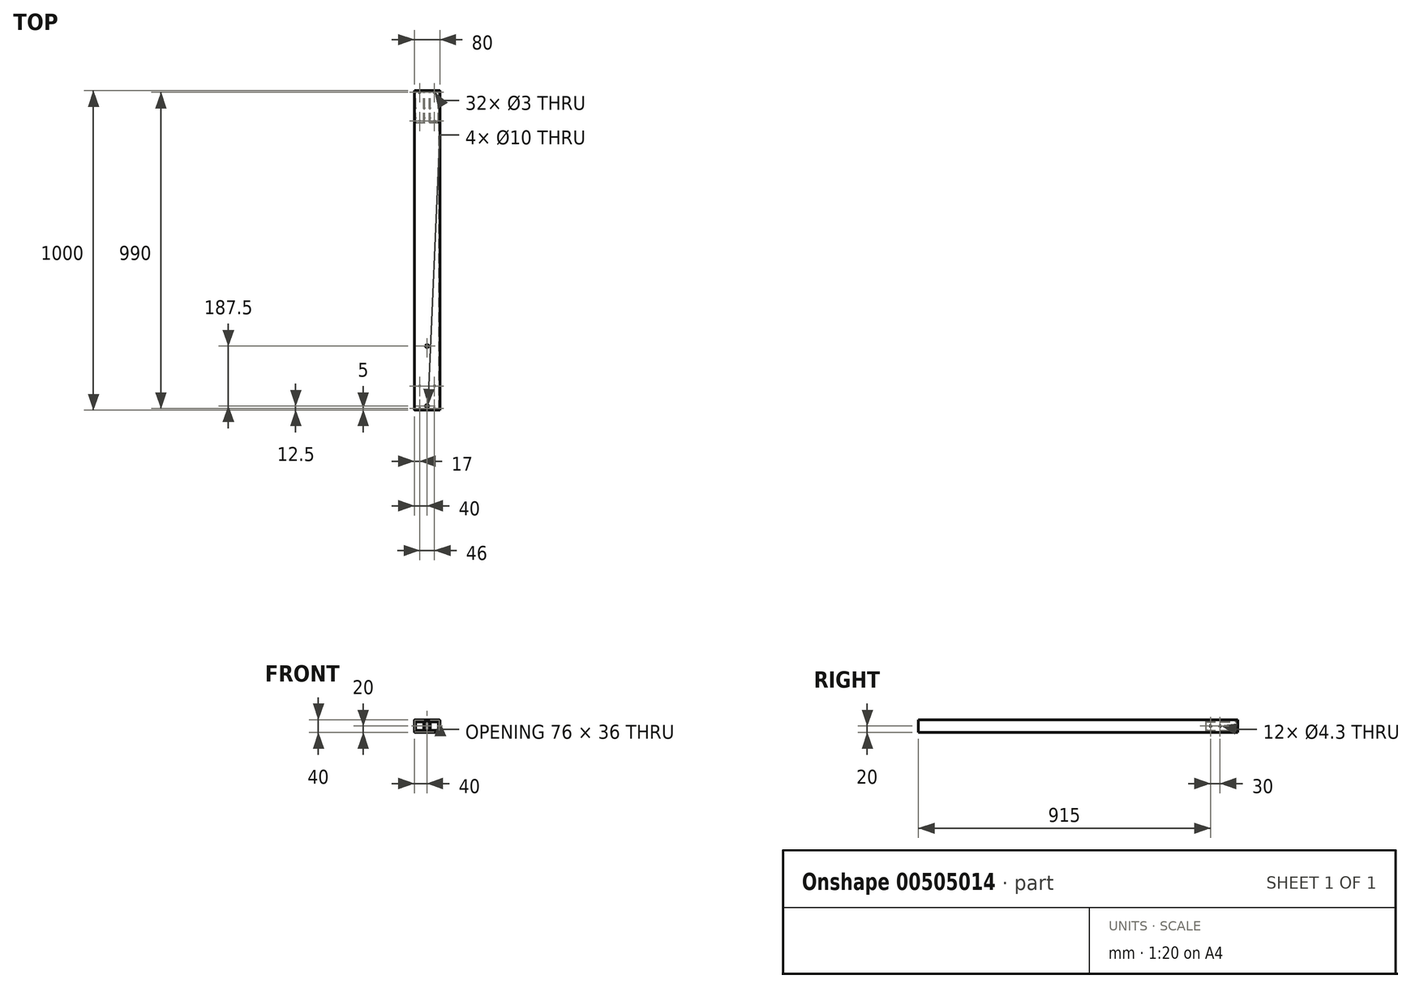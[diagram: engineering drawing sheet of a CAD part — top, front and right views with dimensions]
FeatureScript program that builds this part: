
annotation { "Feature Type Name" : "Feature", "Feature Type Description" : "" }
export const myFeature = defineFeature(function(context is Context, id is Id, definition is map)
    precondition{}
    {
        {
            var Q0;
            Q0=qCreatedBy(makeId("Front.planeOp"),FACE);
            var sketch = newSketch(context, id + "F0", { "sketchPlane" : qUnion([Q0])});
            skLineSegment(sketch, "E0.bottom", {"start": v(-38, 20) * mm, "end": v(38, 20) * mm});
            skLineSegment(sketch, "E0.top", {"start": v(-38, -20) * mm, "end": v(38, -20) * mm});
            skLineSegment(sketch, "E0.left", {"start": v(-40, 18) * mm, "end": v(-40, -18) * mm});
            skLineSegment(sketch, "E0.right", {"start": v(40, 18) * mm, "end": v(40, -18) * mm});
            skPoint(sketch, "E1.visualSharp", {"position": v(-38, 18) * mm});
            skPoint(sketch, "E2.visualSharp", {"position": v(38, -18) * mm});
            skPoint(sketch, "E3.visualSharp", {"position": v(-38, -18) * mm});
            skPoint(sketch, "E4.visualSharp", {"position": v(-40, 20) * mm});
            skArc(sketch, "E4.filletArc", {"start": v(-38, 20) * mm, "mid": v(-39.41, 19.41) * mm, "end": v(-40, 18) * mm});
            skPoint(sketch, "E5.visualSharp", {"position": v(40, 20) * mm});
            skArc(sketch, "E5.filletArc", {"start": v(40, 18) * mm, "mid": v(39.41, 19.41) * mm, "end": v(38, 20) * mm});
            skPoint(sketch, "E6.visualSharp", {"position": v(40, -20) * mm});
            skArc(sketch, "E6.filletArc", {"start": v(38, -20) * mm, "mid": v(39.41, -19.41) * mm, "end": v(40, -18) * mm});
            skPoint(sketch, "E7.visualSharp", {"position": v(-40, -20) * mm});
            skArc(sketch, "E7.filletArc", {"start": v(-40, -18) * mm, "mid": v(-39.41, -19.41) * mm, "end": v(-38, -20) * mm});
            skLineSegment(sketch, "E8.bottom", {"start": v(-37, 18) * mm, "end": v(37, 18) * mm});
            skLineSegment(sketch, "E8.top", {"start": v(-37, -18) * mm, "end": v(37, -18) * mm});
            skLineSegment(sketch, "E8.left", {"start": v(-38, 17) * mm, "end": v(-38, -17) * mm});
            skLineSegment(sketch, "E8.right", {"start": v(38, 17) * mm, "end": v(38, -17) * mm});
            skArc(sketch, "E9.filletArc", {"start": v(-37, 18) * mm, "mid": v(-37.7, 17.7) * mm, "end": v(-38, 17) * mm});
            skArc(sketch, "E10.filletArc", {"start": v(-38, -17) * mm, "mid": v(-37.7, -17.7) * mm, "end": v(-37, -18) * mm});
            skArc(sketch, "E11.filletArc", {"start": v(37, -18) * mm, "mid": v(37.7, -17.7) * mm, "end": v(38, -17) * mm});
            skArc(sketch, "E12.filletArc", {"start": v(38, 17) * mm, "mid": v(37.7, 17.7) * mm, "end": v(37, 18) * mm});
            skPoint(sketch, "E13", {"position": v(0, 0) * mm});
            skSolve(sketch);
        }
        {
            var Q0;
            Q0=makeQuery(id+"F0.imprint","IMPRINT",FACE,{"disambiguationData":[TD([[makeQuery(id+"F0.imprint","IMPRINT",EDGE,{"derivedFrom":sQuery(id+"F0.wireOp",EDGE,"E0.bottom")}),-1.0]])]});
            var Q1;
            {var subQ0=sQuery(id+"F0.wireOp",EDGE,"d41scRek-im4C-Z6XJ-NA7b-lybMWtBvQDZa.bottom");var subQ1=sQuery(id+"F0.wireOp",EDGE,"E1.filletArc");var subQ2=makeQuery(id+"F0.imprint","INTERSECT",VERTEX,{"derivedFrom":[subQ1,subQ0]});Q1=makeQuery(id+"F0.imprint","IMPRINT",FACE,{"disambiguationData":[TD([[makeQuery(id+"F0.imprint","IMPRINT",EDGE,{"disambiguationData":[TD([[subQ2,-1.0]])],"derivedFrom":subQ1}),-1.0]])]});}
            var Q2;
            {var subQ0=sQuery(id+"F0.wireOp",EDGE,"d41scRek-im4C-Z6XJ-NA7b-lybMWtBvQDZa.right");var subQ1=sQuery(id+"F0.wireOp",EDGE,"49b38d49-dcaf-4ad4-8bbf-e22f50cbbb73.filletArc");var subQ2=makeQuery(id+"F0.imprint","INTERSECT",VERTEX,{"derivedFrom":[subQ1,subQ0]});Q2=makeQuery(id+"F0.imprint","IMPRINT",FACE,{"disambiguationData":[TD([[makeQuery(id+"F0.imprint","IMPRINT",EDGE,{"disambiguationData":[TD([[subQ2,-1.0]])],"derivedFrom":subQ1}),-1.0]])]});}
            var Q3;
            {var subQ0=sQuery(id+"F0.wireOp",EDGE,"7cdcf8cc-6b16-4f10-b10a-e8f9950829020.MirrorCS");var subQ1=sQuery(id+"F0.wireOp",EDGE,"E2.filletArc");var subQ2=makeQuery(id+"F0.imprint","INTERSECT",VERTEX,{"derivedFrom":[subQ1,subQ0]});Q3=makeQuery(id+"F0.imprint","IMPRINT",FACE,{"disambiguationData":[TD([[makeQuery(id+"F0.imprint","IMPRINT",EDGE,{"disambiguationData":[TD([[subQ2,-1.0]])],"derivedFrom":subQ1}),-1.0]])]});}
            var Q4;
            {var subQ0=sQuery(id+"F0.wireOp",EDGE,"daf54ab9-f530-4c55-a2cd-1cfbda922d990.MirrorCS");var subQ1=sQuery(id+"F0.wireOp",EDGE,"E3.filletArc");var subQ2=makeQuery(id+"F0.imprint","INTERSECT",VERTEX,{"derivedFrom":[subQ1,subQ0]});Q4=makeQuery(id+"F0.imprint","IMPRINT",FACE,{"disambiguationData":[TD([[makeQuery(id+"F0.imprint","IMPRINT",EDGE,{"disambiguationData":[TD([[subQ2,-1.0]])],"derivedFrom":subQ1}),-1.0]])]});}
            var Q5;
            {var subQ4=sQuery(id+"F0.wireOp",EDGE,"E0.right");Q5=makeQuery(id+"F0.imprint","IMPRINT",FACE,{"disambiguationData":[TD([[makeQuery(id+"F0.imprint","IMPRINT",EDGE,{"derivedFrom":subQ4}),-1.0]])]});}
            var Q6;
            {var subQ1=sQuery(id+"F0.wireOp",EDGE,"E0.top");Q6=makeQuery(id+"F0.imprint","IMPRINT",FACE,{"disambiguationData":[TD([[makeQuery(id+"F0.imprint","IMPRINT",EDGE,{"derivedFrom":subQ1}),1.0]])]});}
            var Q7;
            {var subQ1=sQuery(id+"F0.wireOp",EDGE,"E0.left");Q7=makeQuery(id+"F0.imprint","IMPRINT",FACE,{"disambiguationData":[TD([[makeQuery(id+"F0.imprint","IMPRINT",EDGE,{"derivedFrom":subQ1}),1.0]])]});}
            extrude(context, id + "F1", {"entities" : qUnion([Q0, Q1, Q2, Q3, Q4, Q5, Q6, Q7]), "depth" : 1000 * mm, "offsetDistance" : 25 * mm});
        }
        {
            var Q0;
            Q0=qCreatedBy(makeId("Front.planeOp"),FACE);
            cPlane(context, id + "F2", {"entities" : qUnion([Q0]), "cplaneType" : CPlaneType.OFFSET, "offset" : 1000 * mm, "width" : 150 * mm, "height" : 150 * mm});
        }
        {
            var Q0;
            Q0=qCreatedBy(makeId("Right.planeOp"),FACE);
            var sketch = newSketch(context, id + "F3", { "sketchPlane" : qUnion([Q0])});
            skPoint(sketch, "E14", {"position": v(-1000, 0) * mm});
            skSolve(sketch);
        }
        {
            var Q0;
            Q0=qCreatedBy(makeId("Front.planeOp"),FACE);
            var sketch = newSketch(context, id + "F4", { "sketchPlane" : qUnion([Q0])});
            skLineSegment(sketch, "E15.bottom", {"start": v(-36.5, 18) * mm, "end": v(36.5, 18) * mm});
            skLineSegment(sketch, "E15.top", {"start": v(-36.5, 15) * mm, "end": v(36.5, 15) * mm});
            skLineSegment(sketch, "E15.left", {"start": v(-38, 16.5) * mm, "end": v(-38, 16.5) * mm});
            skLineSegment(sketch, "E15.right", {"start": v(38, 16.5) * mm, "end": v(38, 16.5) * mm});
            skPoint(sketch, "E16.visualSharp", {"position": v(-38, 18) * mm});
            skArc(sketch, "E16.filletArc", {"start": v(-36.5, 18) * mm, "mid": v(-37.56, 17.56) * mm, "end": v(-38, 16.5) * mm});
            skPoint(sketch, "E17.visualSharp", {"position": v(-38, 15) * mm});
            skArc(sketch, "E17.filletArc", {"start": v(-38, 16.5) * mm, "mid": v(-37.56, 15.44) * mm, "end": v(-36.5, 15) * mm});
            skPoint(sketch, "E18.visualSharp", {"position": v(38, 18) * mm});
            skArc(sketch, "E18.filletArc", {"start": v(38, 16.5) * mm, "mid": v(37.56, 17.56) * mm, "end": v(36.5, 18) * mm});
            skPoint(sketch, "E19.visualSharp", {"position": v(38, 15) * mm});
            skArc(sketch, "E19.filletArc", {"start": v(36.5, 15) * mm, "mid": v(37.56, 15.44) * mm, "end": v(38, 16.5) * mm});
            skLineSegment(sketch, "E20.MirrorCS", {"start": v(-36.5, -18) * mm, "end": v(36.5, -18) * mm});
            skArc(sketch, "E21.MirrorCS", {"start": v(-36.5, -18) * mm, "mid": v(-37.56, -17.56) * mm, "end": v(-38, -16.5) * mm});
            skArc(sketch, "E22.MirrorCS", {"start": v(-38, -16.5) * mm, "mid": v(-37.56, -15.44) * mm, "end": v(-36.5, -15) * mm});
            skLineSegment(sketch, "E23.MirrorCS", {"start": v(-36.5, -15) * mm, "end": v(36.5, -15) * mm});
            skArc(sketch, "E24.MirrorCS", {"start": v(36.5, -15) * mm, "mid": v(37.56, -15.44) * mm, "end": v(38, -16.5) * mm});
            skArc(sketch, "E25.MirrorCS", {"start": v(38, -16.5) * mm, "mid": v(37.56, -17.56) * mm, "end": v(36.5, -18) * mm});
            skSolve(sketch);
        }
        {
            var Q0;
            Q0=makeQuery(id+"F4.imprint","IMPRINT",FACE,{"disambiguationData":[TD([[makeQuery(id+"F4.imprint","IMPRINT",EDGE,{"derivedFrom":sQuery(id+"F4.wireOp",EDGE,"E15.bottom")}),-1.0]])]});
            var Q1;
            Q1=makeQuery(id+"F4.imprint","IMPRINT",FACE,{"disambiguationData":[TD([[makeQuery(id+"F4.imprint","IMPRINT",EDGE,{"derivedFrom":sQuery(id+"F4.wireOp",EDGE,"E20.MirrorCS")}),1.0]])]});
            extrude(context, id + "F5", {"entities" : qUnion([Q0, Q1]), "depth" : 100 * mm, "offsetDistance" : 25 * mm});
        }
        {
            var Q0;
            Q0=qCreatedBy(makeId("Front.planeOp"),FACE);
            var sketch = newSketch(context, id + "F6", { "sketchPlane" : qUnion([Q0])});
            skLineSegment(sketch, "E26.bottom", {"start": v(-36, 15) * mm, "end": v(-10, 15) * mm});
            skLineSegment(sketch, "E26.top", {"start": v(-36, -15) * mm, "end": v(-10, -15) * mm});
            skLineSegment(sketch, "E26.left", {"start": v(-38, 13) * mm, "end": v(-38, -13) * mm});
            skLineSegment(sketch, "E26.right", {"start": v(-8, 13) * mm, "end": v(-8, -13) * mm});
            skPoint(sketch, "E27.visualSharp", {"position": v(-38, 15) * mm});
            skArc(sketch, "E27.filletArc", {"start": v(-36, 15) * mm, "mid": v(-37.41, 14.41) * mm, "end": v(-38, 13) * mm});
            skPoint(sketch, "E28.visualSharp", {"position": v(-8, 15) * mm});
            skArc(sketch, "E28.filletArc", {"start": v(-8, 13) * mm, "mid": v(-8.59, 14.41) * mm, "end": v(-10, 15) * mm});
            skPoint(sketch, "E29.visualSharp", {"position": v(-8, -15) * mm});
            skArc(sketch, "E29.filletArc", {"start": v(-10, -15) * mm, "mid": v(-8.59, -14.41) * mm, "end": v(-8, -13) * mm});
            skPoint(sketch, "E30.visualSharp", {"position": v(-38, -15) * mm});
            skArc(sketch, "E30.filletArc", {"start": v(-38, -13) * mm, "mid": v(-37.41, -14.41) * mm, "end": v(-36, -15) * mm});
            skLineSegment(sketch, "E31.0", {"start": v(-35, 13) * mm, "end": v(-11, 13) * mm});
            skLineSegment(sketch, "E31.1", {"start": v(-36, 12) * mm, "end": v(-36, -12) * mm});
            skLineSegment(sketch, "E31.2", {"start": v(-35, -13) * mm, "end": v(-11, -13) * mm});
            skLineSegment(sketch, "E31.3", {"start": v(-10, 12) * mm, "end": v(-10, -12) * mm});
            skArc(sketch, "E32.filletArc", {"start": v(-35, 13) * mm, "mid": v(-35.7, 12.7) * mm, "end": v(-36, 12) * mm});
            skArc(sketch, "E33.filletArc", {"start": v(-10, 12) * mm, "mid": v(-10.3, 12.7) * mm, "end": v(-11, 13) * mm});
            skArc(sketch, "E34.filletArc", {"start": v(-11, -13) * mm, "mid": v(-10.3, -12.7) * mm, "end": v(-10, -12) * mm});
            skArc(sketch, "E35.filletArc", {"start": v(-36, -12) * mm, "mid": v(-35.7, -12.7) * mm, "end": v(-35, -13) * mm});
            skLineSegment(sketch, "E36.MirrorCS", {"start": v(8, 13) * mm, "end": v(8, -13) * mm});
            skArc(sketch, "E37.MirrorCS", {"start": v(8, 13) * mm, "mid": v(8.59, 14.41) * mm, "end": v(10, 15) * mm});
            skLineSegment(sketch, "E38.MirrorCS", {"start": v(36, 15) * mm, "end": v(10, 15) * mm});
            skArc(sketch, "E39.MirrorCS", {"start": v(36, 15) * mm, "mid": v(37.41, 14.41) * mm, "end": v(38, 13) * mm});
            skLineSegment(sketch, "E40.MirrorCS", {"start": v(38, 13) * mm, "end": v(38, -13) * mm});
            skArc(sketch, "E41.MirrorCS", {"start": v(38, -13) * mm, "mid": v(37.41, -14.41) * mm, "end": v(36, -15) * mm});
            skLineSegment(sketch, "E42.MirrorCS", {"start": v(36, -15) * mm, "end": v(10, -15) * mm});
            skArc(sketch, "E43.MirrorCS", {"start": v(10, -15) * mm, "mid": v(8.59, -14.41) * mm, "end": v(8, -13) * mm});
            skArc(sketch, "E44.MirrorCS", {"start": v(11, -13) * mm, "mid": v(10.3, -12.7) * mm, "end": v(10, -12) * mm});
            skLineSegment(sketch, "E45.MirrorCS", {"start": v(10, 12) * mm, "end": v(10, -12) * mm});
            skArc(sketch, "E46.MirrorCS", {"start": v(10, 12) * mm, "mid": v(10.3, 12.7) * mm, "end": v(11, 13) * mm});
            skLineSegment(sketch, "E47.MirrorCS", {"start": v(35, 13) * mm, "end": v(11, 13) * mm});
            skArc(sketch, "E48.MirrorCS", {"start": v(35, 13) * mm, "mid": v(35.7, 12.7) * mm, "end": v(36, 12) * mm});
            skLineSegment(sketch, "E49.MirrorCS", {"start": v(36, 12) * mm, "end": v(36, -12) * mm});
            skArc(sketch, "E50.MirrorCS", {"start": v(36, -12) * mm, "mid": v(35.7, -12.7) * mm, "end": v(35, -13) * mm});
            skLineSegment(sketch, "E51.MirrorCS", {"start": v(35, -13) * mm, "end": v(11, -13) * mm});
            skSolve(sketch);
        }
        {
            var Q0;
            Q0=makeQuery(id+"F6.imprint","IMPRINT",FACE,{"disambiguationData":[TD([[makeQuery(id+"F6.imprint","IMPRINT",EDGE,{"derivedFrom":sQuery(id+"F6.wireOp",EDGE,"E26.bottom")}),-1.0]])]});
            var Q1;
            Q1=makeQuery(id+"F6.imprint","IMPRINT",FACE,{"disambiguationData":[TD([[makeQuery(id+"F6.imprint","IMPRINT",EDGE,{"derivedFrom":sQuery(id+"F6.wireOp",EDGE,"E36.MirrorCS")}),1.0]])]});
            extrude(context, id + "F7", {"entities" : qUnion([Q0, Q1]), "depth" : 100 * mm, "offsetDistance" : 25 * mm});
        }
        {
            var Q0;
            Q0=makeQuery(id+"F7.opExtrude","CAP_FACE",FACE,{"disambiguationData":[OSD([sQuery(id+"F6.wireOp",EDGE,"E26.bottom"),sQuery(id+"F6.wireOp",EDGE,"E26.top"),sQuery(id+"F6.wireOp",EDGE,"E26.left"),sQuery(id+"F6.wireOp",EDGE,"E26.right"),sQuery(id+"F6.wireOp",EDGE,"E27.filletArc"),sQuery(id+"F6.wireOp",EDGE,"E28.filletArc"),sQuery(id+"F6.wireOp",EDGE,"E29.filletArc"),sQuery(id+"F6.wireOp",EDGE,"E30.filletArc"),sQuery(id+"F6.wireOp",EDGE,"E31.0"),sQuery(id+"F6.wireOp",EDGE,"E31.1"),sQuery(id+"F6.wireOp",EDGE,"E31.2"),sQuery(id+"F6.wireOp",EDGE,"E31.3"),sQuery(id+"F6.wireOp",EDGE,"E32.filletArc"),sQuery(id+"F6.wireOp",EDGE,"E33.filletArc"),sQuery(id+"F6.wireOp",EDGE,"E34.filletArc"),sQuery(id+"F6.wireOp",EDGE,"E35.filletArc")])],"isStart":false});
            var Q1;
            Q1=makeQuery(id+"F7.opExtrude","CAP_FACE",FACE,{"disambiguationData":[OSD([sQuery(id+"F6.wireOp",EDGE,"E36.MirrorCS"),sQuery(id+"F6.wireOp",EDGE,"E37.MirrorCS"),sQuery(id+"F6.wireOp",EDGE,"E38.MirrorCS"),sQuery(id+"F6.wireOp",EDGE,"E39.MirrorCS"),sQuery(id+"F6.wireOp",EDGE,"E40.MirrorCS"),sQuery(id+"F6.wireOp",EDGE,"E41.MirrorCS"),sQuery(id+"F6.wireOp",EDGE,"E42.MirrorCS"),sQuery(id+"F6.wireOp",EDGE,"E43.MirrorCS"),sQuery(id+"F6.wireOp",EDGE,"E44.MirrorCS"),sQuery(id+"F6.wireOp",EDGE,"E45.MirrorCS"),sQuery(id+"F6.wireOp",EDGE,"E46.MirrorCS"),sQuery(id+"F6.wireOp",EDGE,"E47.MirrorCS"),sQuery(id+"F6.wireOp",EDGE,"E48.MirrorCS"),sQuery(id+"F6.wireOp",EDGE,"E49.MirrorCS"),sQuery(id+"F6.wireOp",EDGE,"E50.MirrorCS"),sQuery(id+"F6.wireOp",EDGE,"E51.MirrorCS")])],"isStart":false});
            var Q2;
            Q2=makeQuery(id+"F5.opExtrude","CAP_FACE",FACE,{"disambiguationData":[OSD([sQuery(id+"F4.wireOp",EDGE,"E15.bottom"),sQuery(id+"F4.wireOp",EDGE,"E15.top"),sQuery(id+"F4.wireOp",EDGE,"E16.filletArc"),sQuery(id+"F4.wireOp",EDGE,"E17.filletArc"),sQuery(id+"F4.wireOp",EDGE,"E18.filletArc"),sQuery(id+"F4.wireOp",EDGE,"E19.filletArc")])],"isStart":false});
            var Q3;
            Q3=makeQuery(id+"F5.opExtrude","CAP_FACE",FACE,{"disambiguationData":[OSD([sQuery(id+"F4.wireOp",EDGE,"E20.MirrorCS"),sQuery(id+"F4.wireOp",EDGE,"E21.MirrorCS"),sQuery(id+"F4.wireOp",EDGE,"E22.MirrorCS"),sQuery(id+"F4.wireOp",EDGE,"E23.MirrorCS"),sQuery(id+"F4.wireOp",EDGE,"E24.MirrorCS"),sQuery(id+"F4.wireOp",EDGE,"E25.MirrorCS")])],"isStart":false});
            fillet(context, id + "F8", {"entities" : qUnion([Q0, Q1, Q2, Q3]), "radius" : 0.5 * mm, "tangentPropagation" : true, "allowEdgeOverflow" : false});
        }
        {
            var Q0;
            Q0=makeQuery(id+"F1.opExtrude","SWEPT_FACE",FACE,{"disambiguationData":[OSD([sQuery(id+"F0.wireOp",EDGE,"E0.right")])]});
            var sketch = newSketch(context, id + "F9", { "sketchPlane" : qUnion([Q0])});
            skLineSegment(sketch, "E52", {"start": v(0, 0) * mm, "end": v(-85, 0) * mm, "construction": true});
            skCircle(sketch, "E53", {"center": v(-85, 0) * mm, "radius": 2.15 * mm});
            skCircle(sketch, "E54", {"center": v(-55, 0) * mm, "radius": 2.15 * mm});
            skPoint(sketch, "E55.centerSnap0", {"position": v(-1000, 0) * mm});
            skSolve(sketch);
        }
        {
            var Q0;
            Q0=makeQuery(id+"F9.imprint","IMPRINT",FACE,{"disambiguationData":[TD([[makeQuery(id+"F9.imprint","IMPRINT",EDGE,{"derivedFrom":sQuery(id+"F9.wireOp",EDGE,"E53")}),1.0]])]});
            var Q1;
            Q1=makeQuery(id+"F9.imprint","IMPRINT",FACE,{"disambiguationData":[TD([[makeQuery(id+"F9.imprint","IMPRINT",EDGE,{"derivedFrom":sQuery(id+"F9.wireOp",EDGE,"E54")}),1.0]])]});
            extrude(context, id + "F10", {"entities" : qUnion([Q0, Q1]), "operationType" : NewBodyOperationType.REMOVE, "endBound" : BoundingType.THROUGH_ALL, "oppositeDirection" : true, "depth" : 100 * mm, "offsetDistance" : 25 * mm});
        }
        {
            var Q0;
            Q0=makeQuery(id+"F1.opExtrude","SWEPT_FACE",FACE,{"disambiguationData":[OSD([sQuery(id+"F0.wireOp",EDGE,"E0.bottom")])]});
            var sketch = newSketch(context, id + "F11", { "sketchPlane" : qUnion([Q0])});
            skLineSegment(sketch, "E56", {"start": v(-23, -5) * mm, "end": v(23, -5) * mm, "construction": true});
            skLineSegment(sketch, "E57", {"start": v(23, -95) * mm, "end": v(-23, -95) * mm, "construction": true});
            skLineSegment(sketch, "E58", {"start": v(-23, -95) * mm, "end": v(-23, -5) * mm, "construction": true});
            skLineSegment(sketch, "E59", {"start": v(23, -5) * mm, "end": v(23, -95) * mm, "construction": true});
            skCircle(sketch, "E60", {"center": v(-23, -5) * mm, "radius": 1.5 * mm});
            skCircle(sketch, "E61", {"center": v(23, -5) * mm, "radius": 1.5 * mm});
            skCircle(sketch, "E62", {"center": v(23, -95) * mm, "radius": 1.5 * mm});
            skCircle(sketch, "E63", {"center": v(-23, -95) * mm, "radius": 1.5 * mm});
            skLineSegment(sketch, "E64", {"start": v(-38, -995) * mm, "end": v(38, -995) * mm, "construction": true});
            skLineSegment(sketch, "E65", {"start": v(-38, -925) * mm, "end": v(38, -925) * mm, "construction": true});
            skLineSegment(sketch, "E66", {"start": v(-23, -925) * mm, "end": v(-23, -995) * mm, "construction": true});
            skLineSegment(sketch, "E67", {"start": v(23, -925) * mm, "end": v(23, -995) * mm, "construction": true});
            skCircle(sketch, "E68", {"center": v(-23, -925) * mm, "radius": 1.5 * mm});
            skCircle(sketch, "E69", {"center": v(23, -925) * mm, "radius": 1.5 * mm});
            skCircle(sketch, "E70", {"center": v(23, -995) * mm, "radius": 1.5 * mm});
            skCircle(sketch, "E71", {"center": v(-23, -995) * mm, "radius": 1.5 * mm});
            skLineSegment(sketch, "E72", {"start": v(0, -1000) * mm, "end": v(0, -800) * mm, "construction": true});
            skCircle(sketch, "E73", {"center": v(0, -800) * mm, "radius": 5 * mm});
            skCircle(sketch, "E74", {"center": v(0, -987.5) * mm, "radius": 5 * mm});
            skSolve(sketch);
        }
        {
            var Q0;
            Q0=makeQuery(id+"F11.imprint","IMPRINT",FACE,{"disambiguationData":[TD([[makeQuery(id+"F11.imprint","IMPRINT",EDGE,{"derivedFrom":sQuery(id+"F11.wireOp",EDGE,"E60")}),1.0]])]});
            var Q1;
            Q1=makeQuery(id+"F11.imprint","IMPRINT",FACE,{"disambiguationData":[TD([[makeQuery(id+"F11.imprint","IMPRINT",EDGE,{"derivedFrom":sQuery(id+"F11.wireOp",EDGE,"E61")}),1.0]])]});
            var Q2;
            Q2=makeQuery(id+"F11.imprint","IMPRINT",FACE,{"disambiguationData":[TD([[makeQuery(id+"F11.imprint","IMPRINT",EDGE,{"derivedFrom":sQuery(id+"F11.wireOp",EDGE,"E62")}),1.0]])]});
            var Q3;
            Q3=makeQuery(id+"F11.imprint","IMPRINT",FACE,{"disambiguationData":[TD([[makeQuery(id+"F11.imprint","IMPRINT",EDGE,{"derivedFrom":sQuery(id+"F11.wireOp",EDGE,"E63")}),1.0]])]});
            var Q4;
            Q4=makeQuery(id+"F11.imprint","IMPRINT",FACE,{"disambiguationData":[TD([[makeQuery(id+"F11.imprint","IMPRINT",EDGE,{"derivedFrom":sQuery(id+"F11.wireOp",EDGE,"E68")}),1.0]])]});
            var Q5;
            Q5=makeQuery(id+"F11.imprint","IMPRINT",FACE,{"disambiguationData":[TD([[makeQuery(id+"F11.imprint","IMPRINT",EDGE,{"derivedFrom":sQuery(id+"F11.wireOp",EDGE,"E69")}),1.0]])]});
            var Q6;
            Q6=makeQuery(id+"F11.imprint","IMPRINT",FACE,{"disambiguationData":[TD([[makeQuery(id+"F11.imprint","IMPRINT",EDGE,{"derivedFrom":sQuery(id+"F11.wireOp",EDGE,"E71")}),1.0]])]});
            var Q7;
            Q7=makeQuery(id+"F11.imprint","IMPRINT",FACE,{"disambiguationData":[TD([[makeQuery(id+"F11.imprint","IMPRINT",EDGE,{"derivedFrom":sQuery(id+"F11.wireOp",EDGE,"E70")}),1.0]])]});
            var Q8;
            Q8=makeQuery(id+"F11.imprint","IMPRINT",FACE,{"disambiguationData":[TD([[makeQuery(id+"F11.imprint","IMPRINT",EDGE,{"derivedFrom":sQuery(id+"F11.wireOp",EDGE,"E73")}),1.0]])]});
            var Q9;
            Q9=makeQuery(id+"F11.imprint","IMPRINT",FACE,{"disambiguationData":[TD([[makeQuery(id+"F11.imprint","IMPRINT",EDGE,{"derivedFrom":sQuery(id+"F11.wireOp",EDGE,"E74")}),1.0]])]});
            var Q10;
            Q10=sQuery(id+"F11.wireOp",EDGE,"E60");
            var Q11;
            Q11=sQuery(id+"F11.wireOp",EDGE,"E61");
            var Q12;
            Q12=sQuery(id+"F11.wireOp",EDGE,"E62");
            var Q13;
            Q13=sQuery(id+"F11.wireOp",EDGE,"E63");
            extrude(context, id + "F12", {"entities" : qUnion([Q0, Q1, Q2, Q3, Q4, Q5, Q6, Q7, Q8, Q9]), "operationType" : NewBodyOperationType.REMOVE, "surfaceEntities" : qUnion([Q10, Q11, Q12, Q13]), "endBound" : BoundingType.THROUGH_ALL, "oppositeDirection" : true, "depth" : 25 * mm, "offsetDistance" : 25 * mm});
        }
    });
